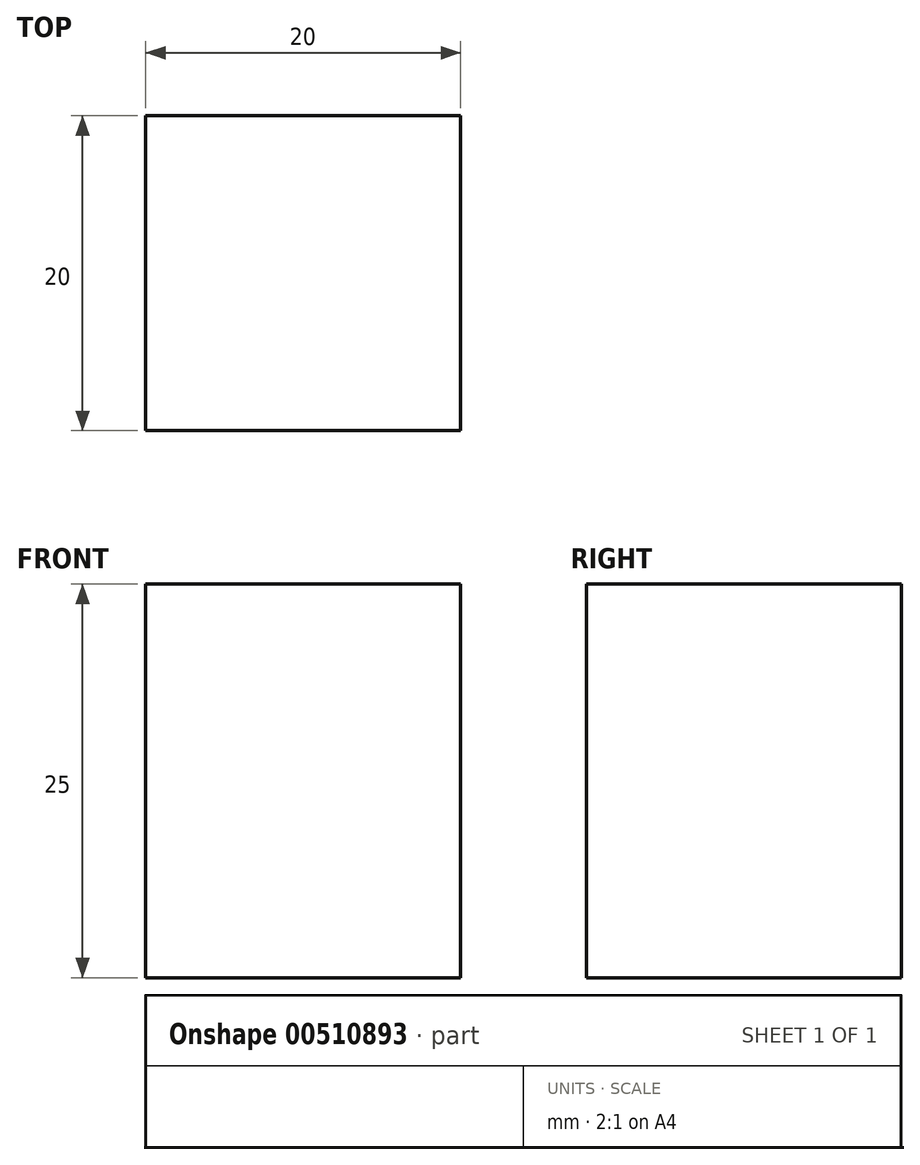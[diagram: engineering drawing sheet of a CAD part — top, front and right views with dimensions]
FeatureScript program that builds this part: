
annotation { "Feature Type Name" : "Feature", "Feature Type Description" : "" }
export const myFeature = defineFeature(function(context is Context, id is Id, definition is map)
    precondition{}
    {
        {
            var Q0;
            Q0=qCreatedBy(makeId("Top.planeOp"),FACE);
            var sketch = newSketch(context, id + "F0", { "sketchPlane" : qUnion([Q0])});
            skLineSegment(sketch, "E0.bottom", {"start": v(-14.83, 20) * mm, "end": v(5.17, 20) * mm});
            skLineSegment(sketch, "E0.top", {"start": v(-14.83, 0) * mm, "end": v(5.17, 0) * mm});
            skLineSegment(sketch, "E0.left", {"start": v(-14.83, 20) * mm, "end": v(-14.83, 0) * mm});
            skLineSegment(sketch, "E0.right", {"start": v(5.17, 20) * mm, "end": v(5.17, 0) * mm});
            skSolve(sketch);
        }
        {
            var Q0;
            Q0=makeQuery(id+"F0.imprint","IMPRINT",FACE,{"disambiguationData":[TD([[makeQuery(id+"F0.imprint","IMPRINT",EDGE,{"derivedFrom":sQuery(id+"F0.wireOp",EDGE,"E0.bottom")}),-1.0]])]});
            extrude(context, id + "F1", {"entities" : qUnion([Q0]), "depth" : 25 * mm});
        }
    });
